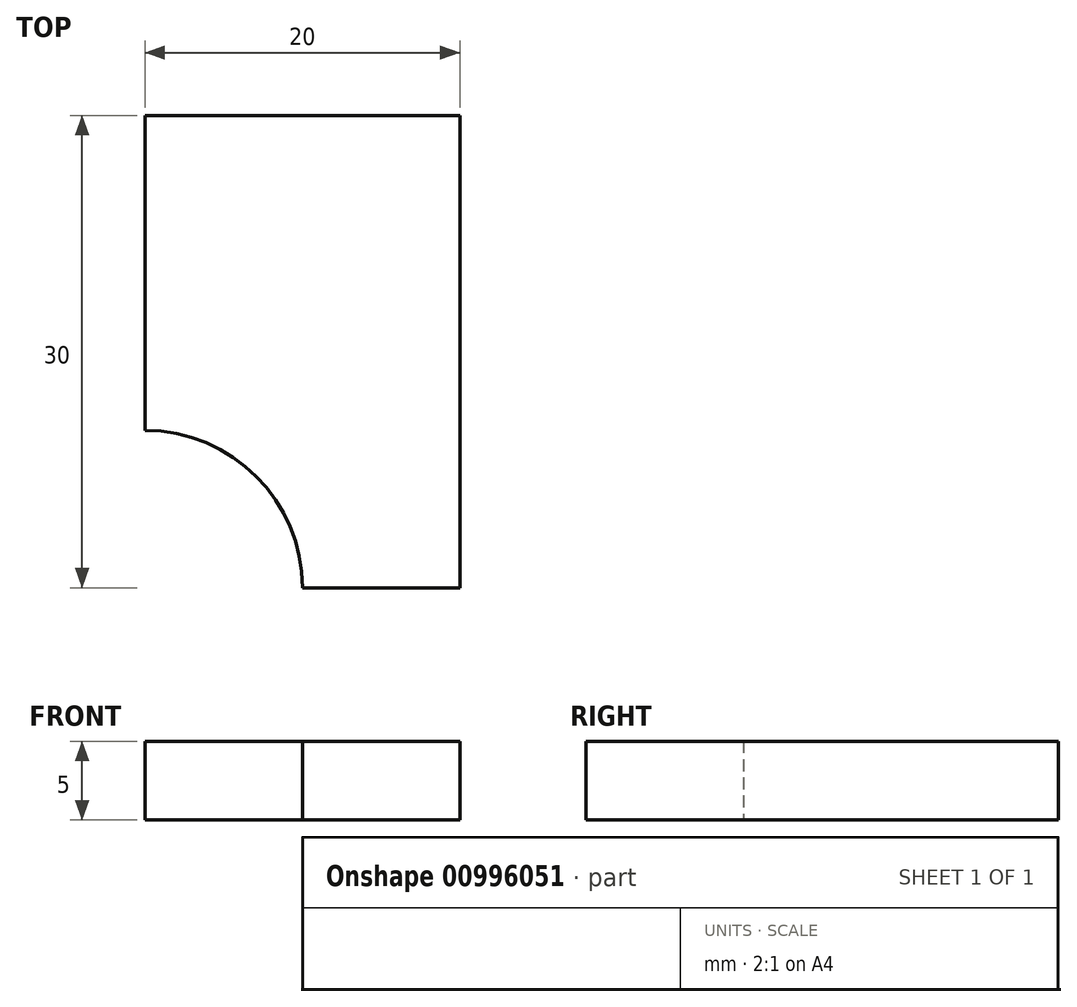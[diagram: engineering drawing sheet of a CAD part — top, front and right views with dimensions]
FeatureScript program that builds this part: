
annotation { "Feature Type Name" : "Feature", "Feature Type Description" : "" }
export const myFeature = defineFeature(function(context is Context, id is Id, definition is map)
    precondition{}
    {
        {
            var Q0;
            Q0=qCreatedBy(makeId("Top.planeOp"),FACE);
            var sketch = newSketch(context, id + "F0", { "sketchPlane" : qUnion([Q0])});
            skLineSegment(sketch, "E0", {"start": v(0, 10) * mm, "end": v(0, 30) * mm});
            skLineSegment(sketch, "E1", {"start": v(0, 30) * mm, "end": v(20, 30) * mm});
            skLineSegment(sketch, "E2", {"start": v(20, 30) * mm, "end": v(20, 0) * mm});
            skLineSegment(sketch, "E3", {"start": v(20, 0) * mm, "end": v(10, 0) * mm});
            skArc(sketch, "E4", {"start": v(10, 0) * mm, "mid": v(7.07, 7.07) * mm, "end": v(0, 10) * mm});
            skSolve(sketch);
        }
        {
            var Q0;
            Q0=makeQuery(id+"F0.imprint","IMPRINT",FACE,{"disambiguationData":[TD([[makeQuery(id+"F0.imprint","IMPRINT",EDGE,{"derivedFrom":sQuery(id+"F0.wireOp",EDGE,"E0")}),-1.0]])]});
            extrude(context, id + "F1", {"entities" : qUnion([Q0]), "depth" : 5 * mm, "offsetDistance" : 25 * mm});
        }
    });
